# Revit family: WIR-MOD-GPRS
name_source: partatom
category: Communication Devices
revit_build: Autodesk Revit 2014 (Build: 20130308_1515(x64)
units: mm (PartAtom-declared; Revit-internal decimal feet)

## types (1)
- WIR-MOD-GPRS
    Assembly Code = D5090
    Certifications = Safety: IECEE Certification Bodies Scheme (CB Scheme), UL 60950
Vehicle Usage: E-Mark (UN ECE Regulation 10.04), ISO7637-2, SAE J1455 (Shock & Vibration)
Hazardous Environments: Class 1 Div 2
Environmental: RoHS, REACH, WEEE
    Default Elevation = 48 "
    Description = The wiSCAPE® Gateway Cellular Modem is a secure Ethernet modem ideal for customers requiring 24/7 broadband connectivity. With simple installation and configuration requirements, the Gateway Cellular Modem is designed to handle robust, fixed applications requiring broadband communication speeds and bandwidth.
    Feartures = 4G LTE performance at 2G power consumption (less than 1W in
idle mode)
• Single version for all major North American network operators
• Fully automatic network operator switching: just insert SIM*
• Remote management and configuration
• Meets industrial-grade certifications including Class 1 Div 2,
MIL-STD-810G, IP64 ingress protection
• Five-year limited warranty
    Green = Plastic, Gray
    Housing Material = Paint - Hubbell - Carbon Black
    Manufacturer = Hubbell Control Solutions
    Model = WIR-MOD-GPRS
    Product Documentation Link = https://hubbellcdn.com
    Product Page URL = https://www.hubbell.com
    Red = Paint - Hubbell - Red
    Type Comments = WIR-MOD-GPRS
    URL = https://www.hubbell.com
    Warranty = 5-Years Warranty
    Yellow = Paint - Hubbell _Gold

## geometry (parser evidence)
native form markers: Sweep x3
no freeform markers — native parametric forms only
